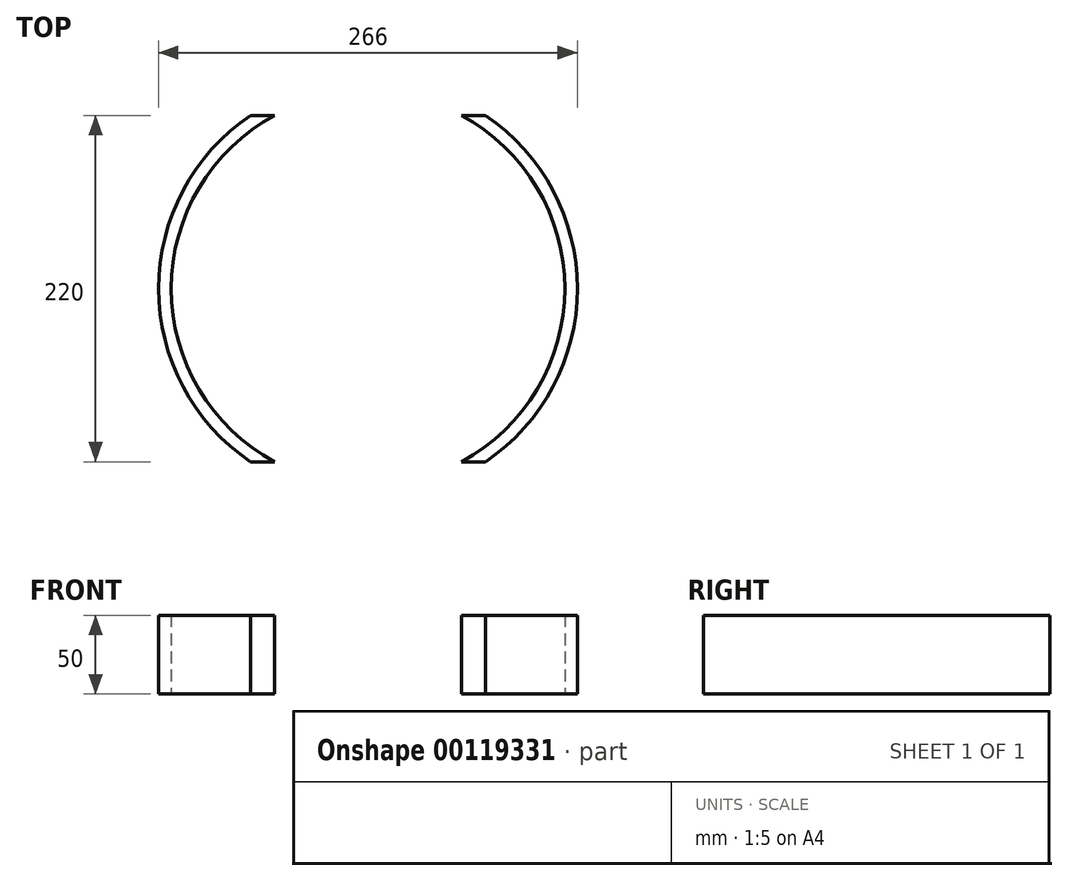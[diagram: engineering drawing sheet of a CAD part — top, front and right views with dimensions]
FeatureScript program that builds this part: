
annotation { "Feature Type Name" : "Feature", "Feature Type Description" : "" }
export const myFeature = defineFeature(function(context is Context, id is Id, definition is map)
    precondition{}
    {
        {
            var Q0;
            Q0=qCreatedBy(makeId("Top.planeOp"),FACE);
            var sketch = newSketch(context, id + "F0", { "sketchPlane" : qUnion([Q0])});
            skArc(sketch, "E0", {"start": v(-168.85, 110) * mm, "mid": v(-234.48, 0) * mm, "end": v(-168.85, -110) * mm});
            skArc(sketch, "E1", {"start": v(-50.1, -110) * mm, "mid": v(15.52, 0) * mm, "end": v(-50.1, 110) * mm});
            skLineSegment(sketch, "E2", {"start": v(-168.85, 110) * mm, "end": v(-184.24, 110) * mm});
            skLineSegment(sketch, "E3", {"start": v(-168.85, -110) * mm, "end": v(-184.24, -110) * mm});
            skLineSegment(sketch, "E4", {"start": v(-50.1, 110) * mm, "end": v(-34.72, 110) * mm});
            skLineSegment(sketch, "E5", {"start": v(-50.1, -110) * mm, "end": v(-34.72, -110) * mm});
            skArc(sketch, "E6", {"start": v(-184.24, 110) * mm, "mid": v(-242.48, 0) * mm, "end": v(-184.24, -110) * mm});
            skArc(sketch, "E7", {"start": v(-34.72, -110) * mm, "mid": v(23.52, 0) * mm, "end": v(-34.72, 110) * mm});
            skSolve(sketch);
        }
        {
            var Q0;
            Q0=makeQuery(id+"F0.imprint","IMPRINT",FACE,{"disambiguationData":[TD([[makeQuery(id+"F0.imprint","IMPRINT",EDGE,{"derivedFrom":sQuery(id+"F0.wireOp",EDGE,"E0")}),-1.0]])]});
            var Q1;
            Q1=makeQuery(id+"F0.imprint","IMPRINT",FACE,{"disambiguationData":[TD([[makeQuery(id+"F0.imprint","IMPRINT",EDGE,{"derivedFrom":sQuery(id+"F0.wireOp",EDGE,"E1")}),-1.0]])]});
            extrude(context, id + "F1", {"entities" : qUnion([Q0, Q1]), "depth" : 50 * mm});
        }
    });
